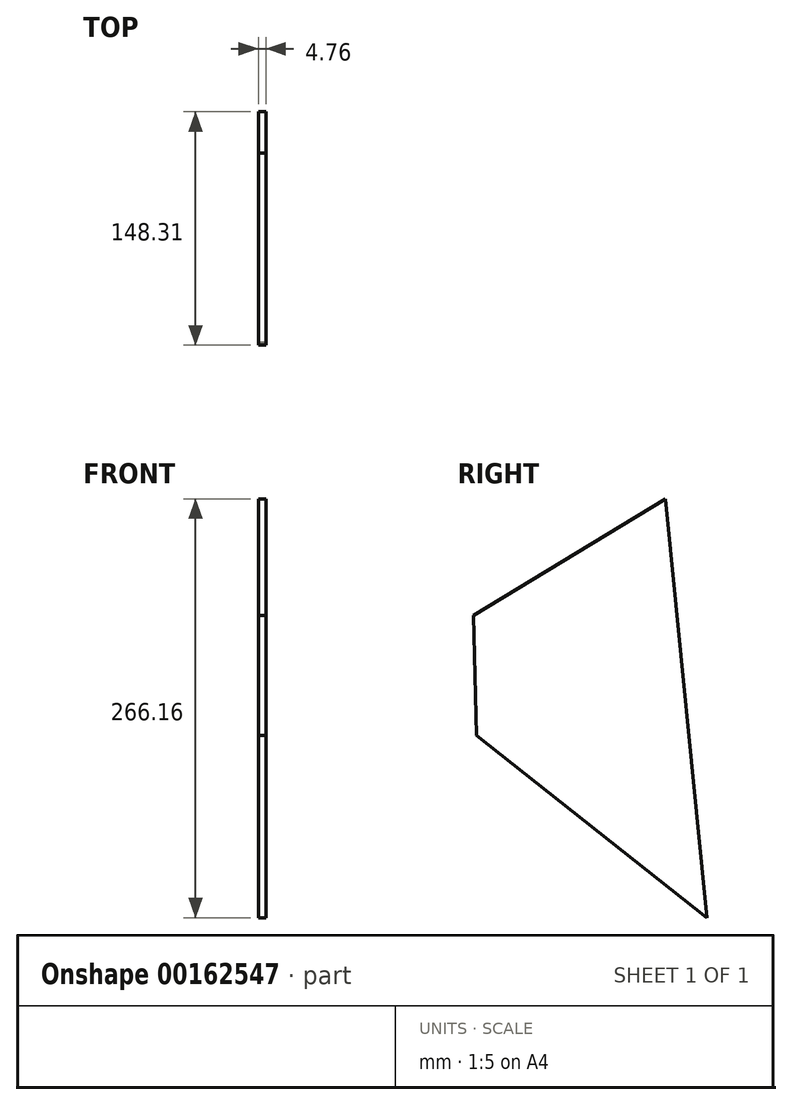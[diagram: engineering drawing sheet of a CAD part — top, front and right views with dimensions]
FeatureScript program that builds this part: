
annotation { "Feature Type Name" : "Feature", "Feature Type Description" : "" }
export const myFeature = defineFeature(function(context is Context, id is Id, definition is map)
    precondition{}
    {
        {
            var Q0;
            Q0=qCreatedBy(makeId("Right.planeOp"),FACE);
            var sketch = newSketch(context, id + "F0", { "sketchPlane" : qUnion([Q0])});
            skLineSegment(sketch, "E0", {"start": v(-121.9, 13.4) * mm, "end": v(0, 87.67) * mm});
            skLineSegment(sketch, "E1", {"start": v(0, 87.67) * mm, "end": v(26.4, -178.49) * mm});
            skLineSegment(sketch, "E2", {"start": v(-120.11, -62.78) * mm, "end": v(26.4, -178.49) * mm});
            skLineSegment(sketch, "E3", {"start": v(-121.9, 13.4) * mm, "end": v(-120.11, -62.78) * mm});
            skSolve(sketch);
        }
        {
            var Q0;
            Q0=qSketchRegion(id+"F0",true);
            extrude(context, id + "F1", {"entities" : qUnion([Q0]), "depth" : 4.76 * mm});
        }
    });
